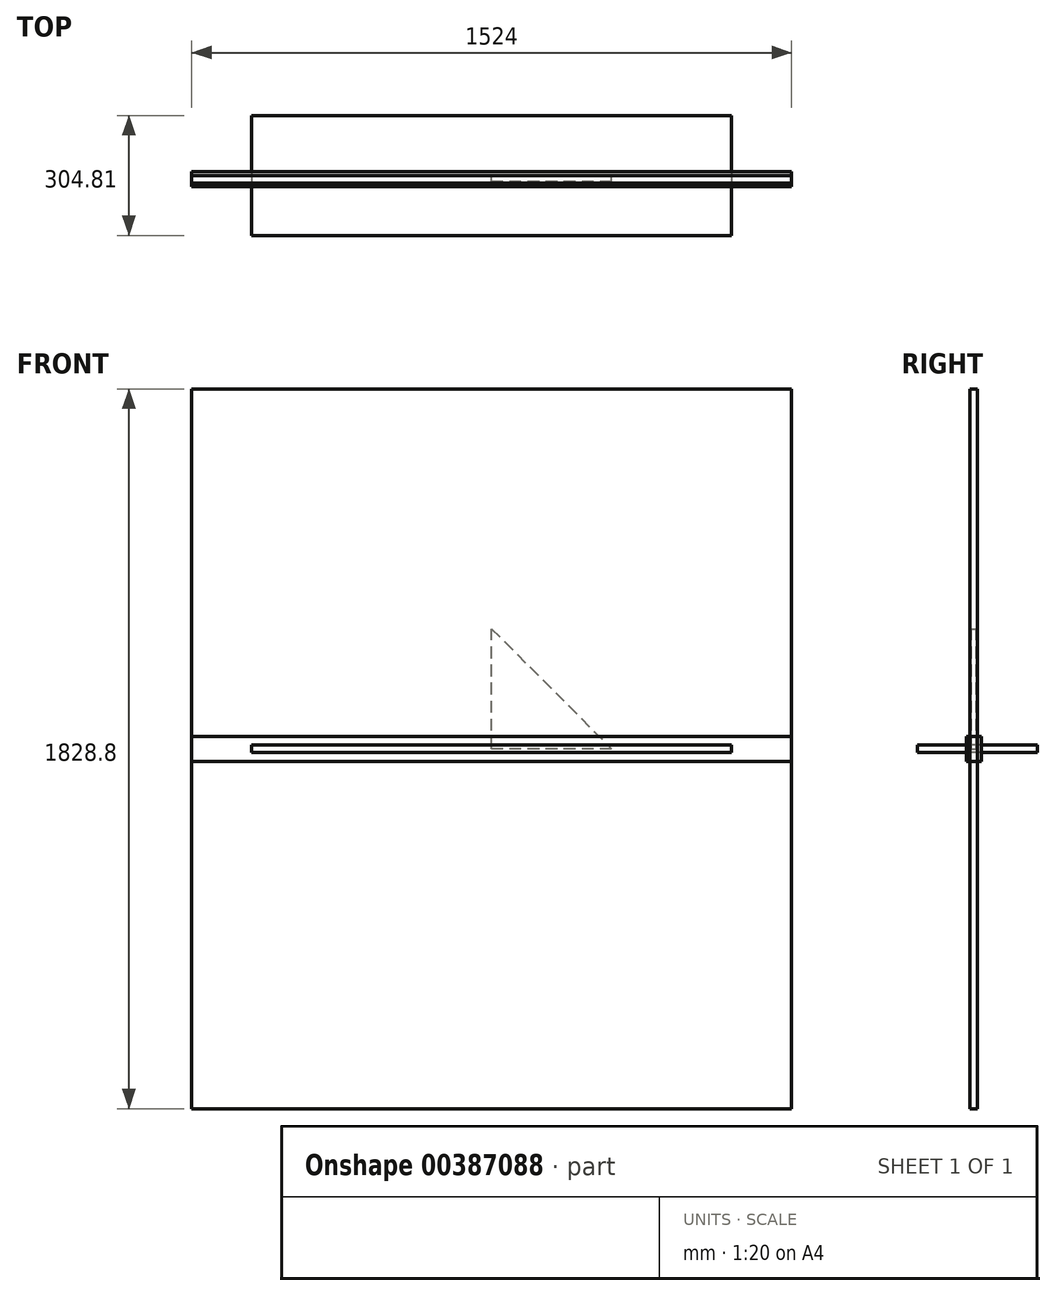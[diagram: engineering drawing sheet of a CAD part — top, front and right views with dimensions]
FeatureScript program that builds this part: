
annotation { "Feature Type Name" : "Feature", "Feature Type Description" : "" }
export const myFeature = defineFeature(function(context is Context, id is Id, definition is map)
    precondition{}
    {
        {
            var Q0;
            Q0=qCreatedBy(makeId("Front.planeOp"),FACE);
            var sketch = newSketch(context, id + "F0", { "sketchPlane" : qUnion([Q0])});
            skLineSegment(sketch, "E0.bottom", {"start": v(-762, 914.4) * mm, "end": v(762, 914.4) * mm});
            skLineSegment(sketch, "E0.top", {"start": v(-762, -914.4) * mm, "end": v(762, -914.4) * mm});
            skLineSegment(sketch, "E0.left", {"start": v(-762, 914.4) * mm, "end": v(-762, -914.4) * mm});
            skLineSegment(sketch, "E0.right", {"start": v(762, 914.4) * mm, "end": v(762, -914.4) * mm});
            skSolve(sketch);
        }
        {
            var Q0;
            Q0 = qSketchRegion(id + "F0", true);
            extrude(context, id + "F1", {"entities" : qUnion([Q0]), "depth" : 19.05 * mm, "symmetric" : true});
        }
        {
            var Q0;
            Q0=qCreatedBy(makeId("Top.planeOp"),FACE);
            var sketch = newSketch(context, id + "F2", { "sketchPlane" : qUnion([Q0])});
            skLineSegment(sketch, "E1.bottom", {"start": v(-609.6, 161.92) * mm, "end": v(609.6, 161.93) * mm});
            skLineSegment(sketch, "E1.top", {"start": v(-609.6, -142.88) * mm, "end": v(609.6, -142.87) * mm});
            skLineSegment(sketch, "E1.left", {"start": v(-609.6, 161.92) * mm, "end": v(-609.6, -142.88) * mm});
            skLineSegment(sketch, "E1.right", {"start": v(609.6, 161.93) * mm, "end": v(609.6, -142.87) * mm});
            skSolve(sketch);
        }
        {
            var Q0;
            Q0 = qSketchRegion(id + "F2", true);
            extrude(context, id + "F3", {"entities" : qUnion([Q0]), "depth" : 19.05 * mm, "symmetric" : true});
        }
        {
            var Q0;
            Q0=qCreatedBy(makeId("Top.planeOp"),FACE);
            var sketch = newSketch(context, id + "F4", { "sketchPlane" : qUnion([Q0])});
            skLineSegment(sketch, "E2.bottom", {"start": v(-762, 19.05) * mm, "end": v(762, 19.05) * mm});
            skLineSegment(sketch, "E2.top", {"start": v(-762, -19.05) * mm, "end": v(762, -19.05) * mm});
            skLineSegment(sketch, "E2.left", {"start": v(-762, 19.05) * mm, "end": v(-762, -19.05) * mm});
            skLineSegment(sketch, "E2.right", {"start": v(762, 19.05) * mm, "end": v(762, -19.05) * mm});
            skSolve(sketch);
        }
        {
            var Q0;
            Q0 = qSketchRegion(id + "F4", true);
            extrude(context, id + "F5", {"entities" : qUnion([Q0]), "depth" : 63.5 * mm, "symmetric" : true});
        }
        {
            var Q0;
            Q0=qCreatedBy(makeId("Front.planeOp"),FACE);
            var sketch = newSketch(context, id + "F6", { "sketchPlane" : qUnion([Q0])});
            skLineSegment(sketch, "E3", {"start": v(0, 0) * mm, "end": v(0, 304.8) * mm});
            skLineSegment(sketch, "E4", {"start": v(0, 304.8) * mm, "end": v(304.8, 0) * mm});
            skLineSegment(sketch, "E5", {"start": v(304.8, 0) * mm, "end": v(0, 0) * mm});
            skSolve(sketch);
        }
        {
            var Q0;
            Q0 = qSketchRegion(id + "F6", true);
            extrude(context, id + "F7", {"entities" : qUnion([Q0]), "depth" : 12.7 * mm, "symmetric" : true});
        }
    });
